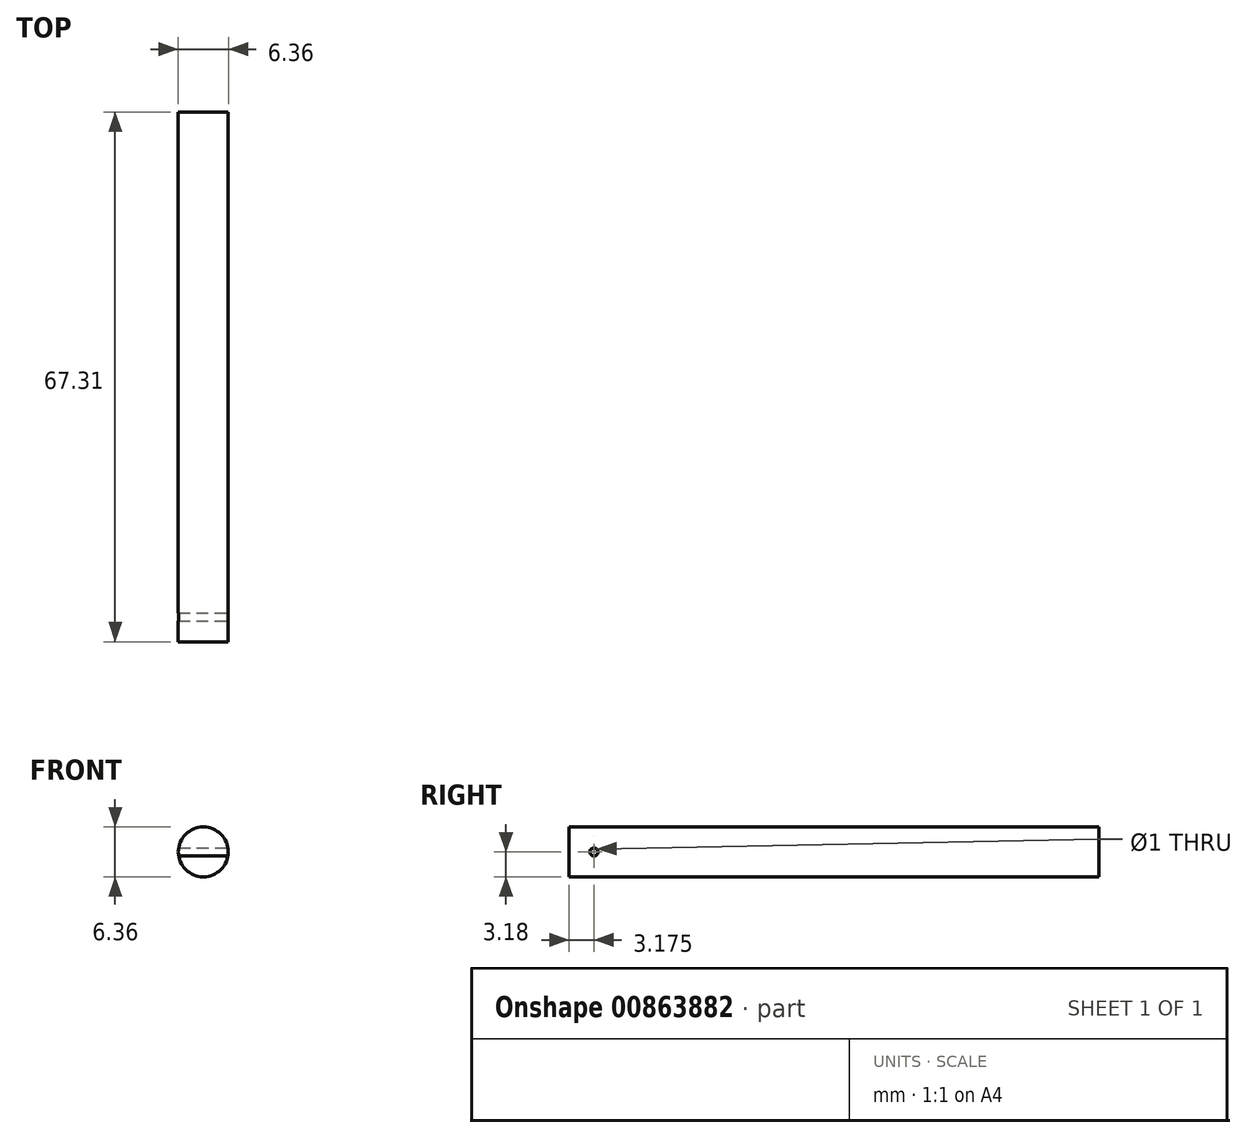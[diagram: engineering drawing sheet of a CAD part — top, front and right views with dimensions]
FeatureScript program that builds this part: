
annotation { "Feature Type Name" : "Feature", "Feature Type Description" : "" }
export const myFeature = defineFeature(function(context is Context, id is Id, definition is map)
    precondition{}
    {
        {
            var Q0;
            Q0=qCreatedBy(makeId("Front.planeOp"),FACE);
            var sketch = newSketch(context, id + "F0", { "sketchPlane" : qUnion([Q0])});
            skCircle(sketch, "E0", {"center": v(0, 0) * mm, "radius": 3.18 * mm});
            skSolve(sketch);
        }
        {
            var Q0;
            Q0 = qSketchRegion(id + "F0", true);
            extrude(context, id + "F1", {"entities" : qUnion([Q0]), "oppositeDirection" : true, "depth" : 67.3 * mm, "offsetDistance" : 25.4 * mm});
        }
        {
            var Q0;
            Q0=qCreatedBy(makeId("Right.planeOp"),FACE);
            var sketch = newSketch(context, id + "F2", { "sketchPlane" : qUnion([Q0])});
            skCircle(sketch, "E1", {"center": v(3.18, 0) * mm, "radius": 0.5 * mm});
            skSolve(sketch);
        }
        {
            var Q0;
            Q0 = qSketchRegion(id + "F2", true);
            extrude(context, id + "F3", {"entities" : qUnion([Q0]), "operationType" : NewBodyOperationType.REMOVE, "oppositeDirection" : true, "depth" : 25.4 * mm, "offsetDistance" : 25.4 * mm, "symmetric" : true});
        }
    });
